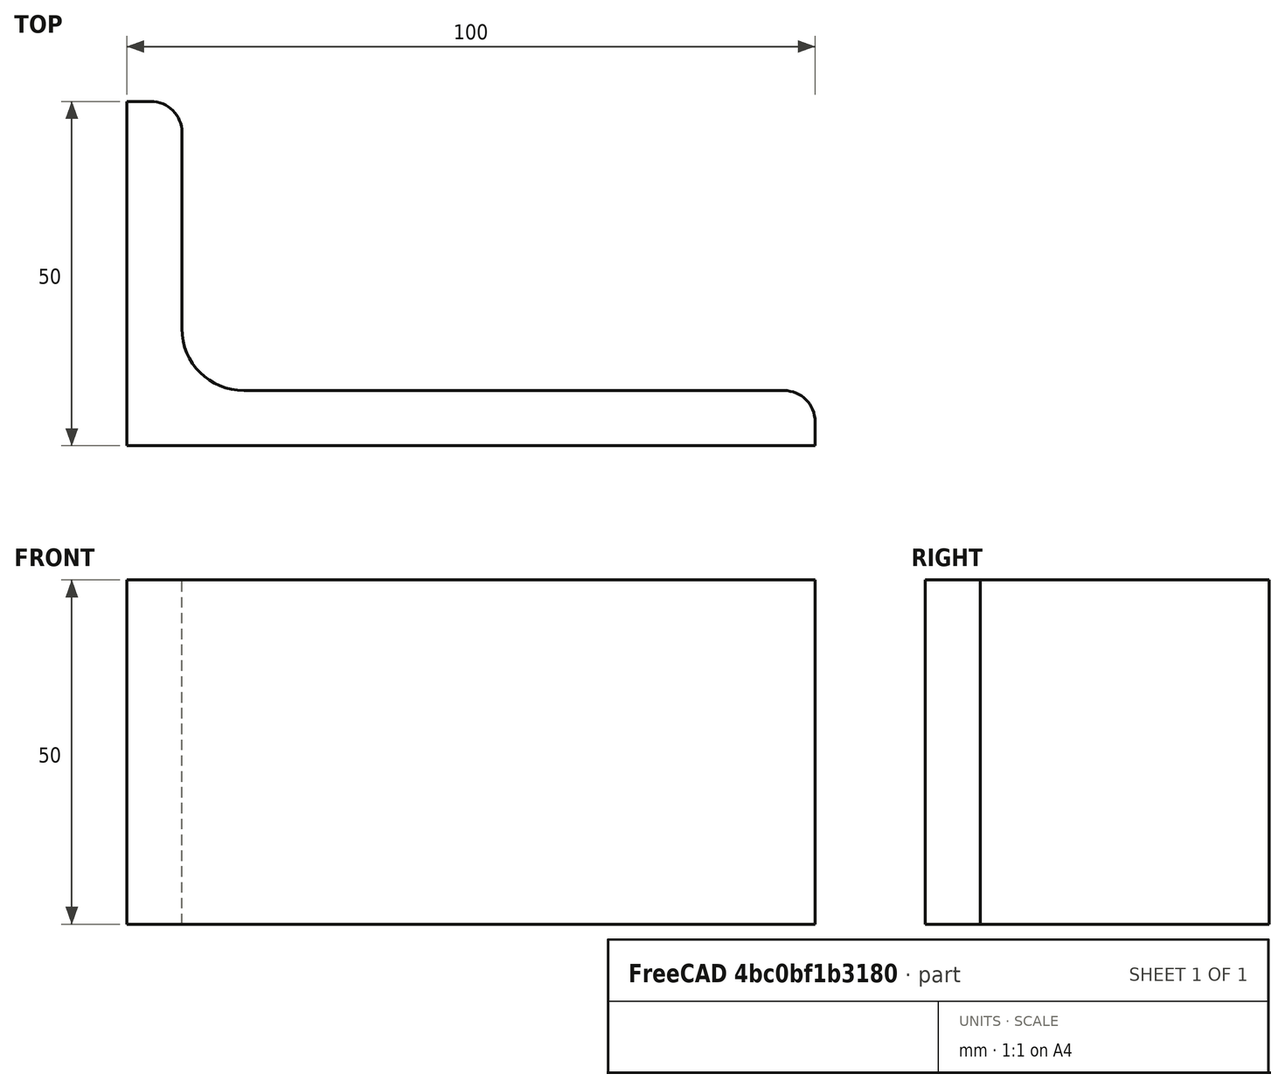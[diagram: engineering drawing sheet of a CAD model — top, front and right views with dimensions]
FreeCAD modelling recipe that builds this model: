
FCSTD DOCUMENT  (FreeCAD 0.15R4671 (Git))
Label: Angle Bar 100x50x8 EN10056 S235JR
License: All rights reserved
LicenseURL: http://en.wikipedia.org/wiki/All_rights_reserved
objects: Sketcher::SketchObject×1, Part::Extrusion×1
note: 2 computed .brp shape members not serialized (recipe doc carries the construction recipe); baked Part::Feature solids carry a one-line shape summary decoded from their .brp

FEATURE [Sketcher::SketchObject] Sketch
  sketch-geometry (9):
    g0: LineSegment StartX=0 StartY=0 StartZ=0 EndX=100 EndY=0 EndZ=0
    g1: LineSegment StartX=100 StartY=0 StartZ=0 EndX=100 EndY=3.5 EndZ=0
    g2: LineSegment StartX=95.5 StartY=8 StartZ=0 EndX=17 EndY=8 EndZ=0
    g3: LineSegment StartX=0 StartY=0 StartZ=0 EndX=0 EndY=50 EndZ=0
    g4: LineSegment StartX=0 StartY=50 StartZ=0 EndX=3.5 EndY=50 EndZ=0
    g5: LineSegment StartX=8 StartY=45.5 StartZ=0 EndX=8 EndY=17 EndZ=0
    g6: ArcOfCircle CenterX=17 CenterY=17 CenterZ=0 NormalX=0 NormalY=0 NormalZ=1 Radius=9 StartAngle=3.14159 EndAngle=4.71239
    g7: ArcOfCircle CenterX=3.5 CenterY=45.5 CenterZ=0 NormalX=0 NormalY=0 NormalZ=1 Radius=4.5 StartAngle=0 EndAngle=1.5708
    g8: ArcOfCircle CenterX=95.5 CenterY=3.5 CenterZ=0 NormalX=0 NormalY=0 NormalZ=1 Radius=4.5 StartAngle=0 EndAngle=1.5708
  constraints (23):
    c: Coincident(g0,g-1)
    c: Horizontal(g0)
    c: Coincident(g1,g0)
    c: Vertical(g1)
    c: Horizontal(g2)
    c: Coincident(g3,g-1)
    c: Vertical(g3)
    c: Coincident(g4,g3)
    c: Horizontal(g4)
    c: Vertical(g5)
    c: Tangent(g5,g6) = -1.5708
    c: Tangent(g2,g6) = 1.5708
    c: Tangent(g4,g7) = 1.5708
    c: Tangent(g5,g7) = 1.5708
    c: Tangent(g2,g8) = -1.5708
    c: Tangent(g1,g8) = -1.5708
    c: DistanceX(g0) = 100
    c: DistanceY(g3) = 50
    c: DistanceY(g0,g2) = 8
    c: DistanceX(g3,g5) = 8
    c: Radius(g6) = 9
    c: Radius(g8) = 4.5
    c: Radius(g7) = 4.5
FEATURE [Part::Extrusion] Extrude  label="Angle Bar 100x50x8 EN10056 S235JR"
  Base = -> Sketch
  Dir = (0,0,50)
  Solid = true
